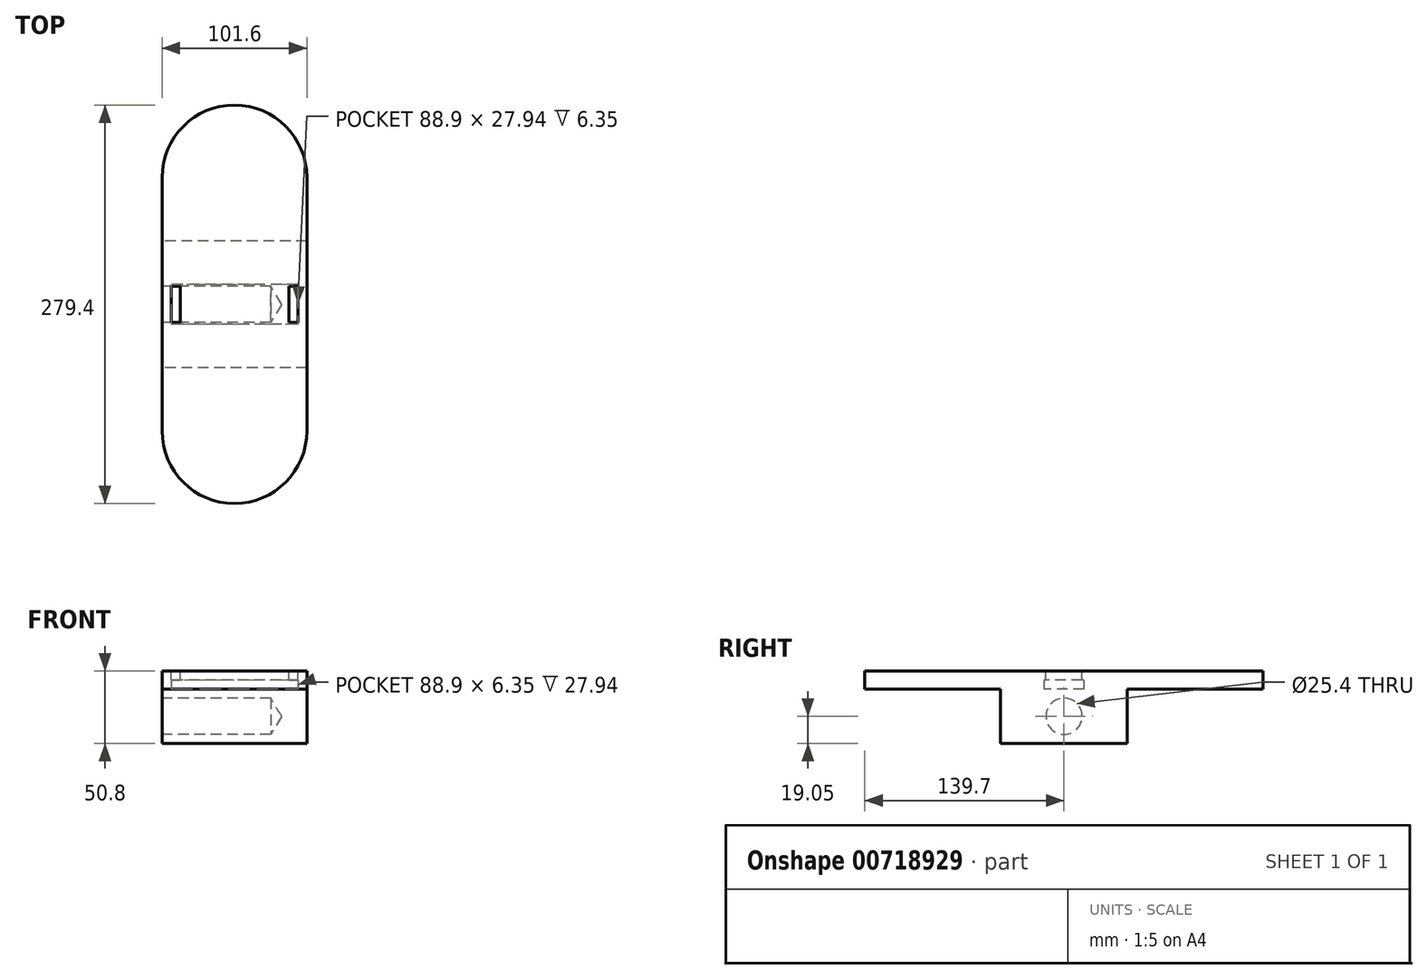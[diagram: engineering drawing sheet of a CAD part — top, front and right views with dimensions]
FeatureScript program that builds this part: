
annotation { "Feature Type Name" : "Feature", "Feature Type Description" : "" }
export const myFeature = defineFeature(function(context is Context, id is Id, definition is map)
    precondition{}
    {
        {
            var Q0;
            Q0=qCreatedBy(makeId("Top.planeOp"),FACE);
            var sketch = newSketch(context, id + "F0", { "sketchPlane" : qUnion([Q0])});
            skLineSegment(sketch, "E0.left", {"start": v(-50.8, -88.9) * mm, "end": v(-50.8, 88.9) * mm});
            skLineSegment(sketch, "E0.right", {"start": v(50.8, -88.9) * mm, "end": v(50.8, 88.9) * mm});
            skPoint(sketch, "E0.middle", {"position": v(0, 0) * mm});
            skArc(sketch, "E1", {"start": v(-50.8, 88.9) * mm, "mid": v(0, 139.7) * mm, "end": v(50.8, 88.9) * mm});
            skArc(sketch, "E2", {"start": v(50.8, -88.9) * mm, "mid": v(0, -139.7) * mm, "end": v(-50.8, -88.9) * mm});
            skSolve(sketch);
        }
        {
            var Q0;
            Q0=makeQuery(id+"F0.imprint","IMPRINT",FACE,{"disambiguationData":[TD([[makeQuery(id+"F0.imprint","IMPRINT",EDGE,{"derivedFrom":sQuery(id+"F0.wireOp",EDGE,"E0.left")}),-1.0]])]});
            extrude(context, id + "F1", {"entities" : qUnion([Q0]), "depth" : 12.7 * mm, "offsetDistance" : 25.4 * mm});
        }
        {
            var Q0;
            Q0=makeQuery(id+"F1.opExtrude","CAP_FACE",FACE,{"disambiguationData":[OSD([sQuery(id+"F0.wireOp",EDGE,"E0.left"),sQuery(id+"F0.wireOp",EDGE,"E0.right"),sQuery(id+"F0.wireOp",EDGE,"E1"),sQuery(id+"F0.wireOp",EDGE,"E2")])],"isStart":true});
            var sketch = newSketch(context, id + "F2", { "sketchPlane" : qUnion([Q0])});
            skLineSegment(sketch, "E3.bottom", {"start": v(50.8, 44.45) * mm, "end": v(-50.8, 44.45) * mm});
            skLineSegment(sketch, "E3.top", {"start": v(50.8, -44.45) * mm, "end": v(-50.8, -44.45) * mm});
            skLineSegment(sketch, "E3.left", {"start": v(50.8, 44.45) * mm, "end": v(50.8, -44.45) * mm});
            skLineSegment(sketch, "E3.right", {"start": v(-50.8, 44.45) * mm, "end": v(-50.8, -44.45) * mm});
            skPoint(sketch, "E3.middle", {"position": v(0, 0) * mm});
            skSolve(sketch);
        }
        {
            var Q0;
            Q0=makeQuery(id+"F2.imprint","IMPRINT",FACE,{"disambiguationData":[TD([[makeQuery(id+"F2.imprint","IMPRINT",EDGE,{"derivedFrom":sQuery(id+"F2.wireOp",EDGE,"E3.bottom")}),1.0]])]});
            extrude(context, id + "F3", {"entities" : qUnion([Q0]), "operationType" : NewBodyOperationType.ADD, "depth" : 38.1 * mm, "offsetDistance" : 25.4 * mm});
        }
        {
            var Q0;
            Q0=makeQuery(id+"F3.boolean.opBoolean","MERGE",FACE,{"derivedFrom":[makeQuery(id+"F1.opExtrude","SWEPT_FACE",FACE,{"disambiguationData":[OSD([sQuery(id+"F0.wireOp",EDGE,"E0.left")])]}),makeQuery(id+"F3.opExtrude","SWEPT_FACE",FACE,{"disambiguationData":[OSD([sQuery(id+"F2.wireOp",EDGE,"E3.right")])]})]});
            var sketch = newSketch(context, id + "F4", { "sketchPlane" : qUnion([Q0])});
            skPoint(sketch, "E4", {"position": v(0, -19.05) * mm});
            skPoint(sketch, "E4.positionSnap0", {"position": v(-44.45, -19.05) * mm});
            skSolve(sketch);
        }
        {
            var Q0;
            Q0=sQuery(id+"F4.wireOp",VERTEX,"E4");
            var Q1;
            Q1=makeQuery(id+"F1.opExtrude","SWEPT_BODY",BODY,{"disambiguationData":[OSD([sQuery(id+"F0.wireOp",EDGE,"E0.left"),sQuery(id+"F0.wireOp",EDGE,"E0.right"),sQuery(id+"F0.wireOp",EDGE,"E1"),sQuery(id+"F0.wireOp",EDGE,"E2")])]});
            hole(context, id + "F5", {"style" : HoleStyle.SIMPLE, "endStyle" : HoleEndStyle.BLIND, "holeDiameter" : 25.4 * mm, "majorDiameter" : 6.35 * mm, "holeDepth" : 76.2 * mm, "isTappedThrough" : true, "tappedDepth" : 12.7 * mm, "tapClearance" : 3, "locations" : qUnion([Q0]), "scope" : qUnion([Q1])});
        }
        {
            var Q0;
            Q0=makeQuery(id+"F1.opExtrude","CAP_FACE",FACE,{"disambiguationData":[OSD([sQuery(id+"F0.wireOp",EDGE,"E0.left"),sQuery(id+"F0.wireOp",EDGE,"E0.right"),sQuery(id+"F0.wireOp",EDGE,"E1"),sQuery(id+"F0.wireOp",EDGE,"E2")])],"isStart":false});
            var sketch = newSketch(context, id + "F6", { "sketchPlane" : qUnion([Q0])});
            skLineSegment(sketch, "E5.bottom", {"start": v(-44.45, 12.7) * mm, "end": v(-38.1, 12.7) * mm});
            skLineSegment(sketch, "E5.top", {"start": v(-44.45, -12.7) * mm, "end": v(-38.1, -12.7) * mm});
            skLineSegment(sketch, "E5.left", {"start": v(-44.45, 12.7) * mm, "end": v(-44.45, -12.7) * mm});
            skLineSegment(sketch, "E5.right", {"start": v(-38.1, 12.7) * mm, "end": v(-38.1, -12.7) * mm});
            skLineSegment(sketch, "E6.bottom", {"start": v(38.1, 12.7) * mm, "end": v(44.45, 12.7) * mm});
            skLineSegment(sketch, "E6.top", {"start": v(38.1, -12.7) * mm, "end": v(44.45, -12.7) * mm});
            skLineSegment(sketch, "E6.left", {"start": v(38.1, 12.7) * mm, "end": v(38.1, -12.7) * mm});
            skLineSegment(sketch, "E6.right", {"start": v(44.45, 12.7) * mm, "end": v(44.45, -12.7) * mm});
            skPoint(sketch, "E7", {"position": v(-38.1, 0) * mm});
            skPoint(sketch, "E8", {"position": v(38.1, 0) * mm});
            skSolve(sketch);
        }
        {
            var Q0;
            Q0=makeQuery(id+"F6.imprint","IMPRINT",FACE,{"disambiguationData":[TD([[makeQuery(id+"F6.imprint","IMPRINT",EDGE,{"derivedFrom":sQuery(id+"F6.wireOp",EDGE,"E5.bottom")}),-1.0]])]});
            var Q1;
            Q1=makeQuery(id+"F6.imprint","IMPRINT",FACE,{"disambiguationData":[TD([[makeQuery(id+"F6.imprint","IMPRINT",EDGE,{"derivedFrom":sQuery(id+"F6.wireOp",EDGE,"E6.bottom")}),-1.0]])]});
            extrude(context, id + "F7", {"entities" : qUnion([Q0, Q1]), "operationType" : NewBodyOperationType.REMOVE, "oppositeDirection" : true, "depth" : 6.35 * mm, "offsetDistance" : 25.4 * mm});
        }
        {
            var Q0;
            Q0=makeQuery(id+"F2.imprint","IMPRINT",FACE,{"disambiguationData":[TD([[makeQuery(id+"F2.imprint","IMPRINT",EDGE,{"derivedFrom":sQuery(id+"F2.wireOp",EDGE,"E3.bottom")}),1.0]])]});
            var sketch = newSketch(context, id + "F8", { "sketchPlane" : qUnion([Q0])});
            skLineSegment(sketch, "E9.bottom", {"start": v(44.45, -13.97) * mm, "end": v(-44.45, -13.97) * mm});
            skLineSegment(sketch, "E9.top", {"start": v(44.45, 13.97) * mm, "end": v(-44.45, 13.97) * mm});
            skLineSegment(sketch, "E9.left", {"start": v(44.45, -13.97) * mm, "end": v(44.45, 13.97) * mm});
            skLineSegment(sketch, "E9.right", {"start": v(-44.45, -13.97) * mm, "end": v(-44.45, 13.97) * mm});
            skPoint(sketch, "E9.middle", {"position": v(0, 0) * mm});
            skSolve(sketch);
        }
        {
            var Q0;
            Q0=makeQuery(id+"F8.imprint","IMPRINT",FACE,{"disambiguationData":[TD([[makeQuery(id+"F8.imprint","IMPRINT",EDGE,{"derivedFrom":sQuery(id+"F8.wireOp",EDGE,"E9.bottom")}),-1.0]])]});
            extrude(context, id + "F9", {"entities" : qUnion([Q0]), "operationType" : NewBodyOperationType.REMOVE, "oppositeDirection" : true, "depth" : 6.35 * mm, "offsetDistance" : 25.4 * mm});
        }
    });
